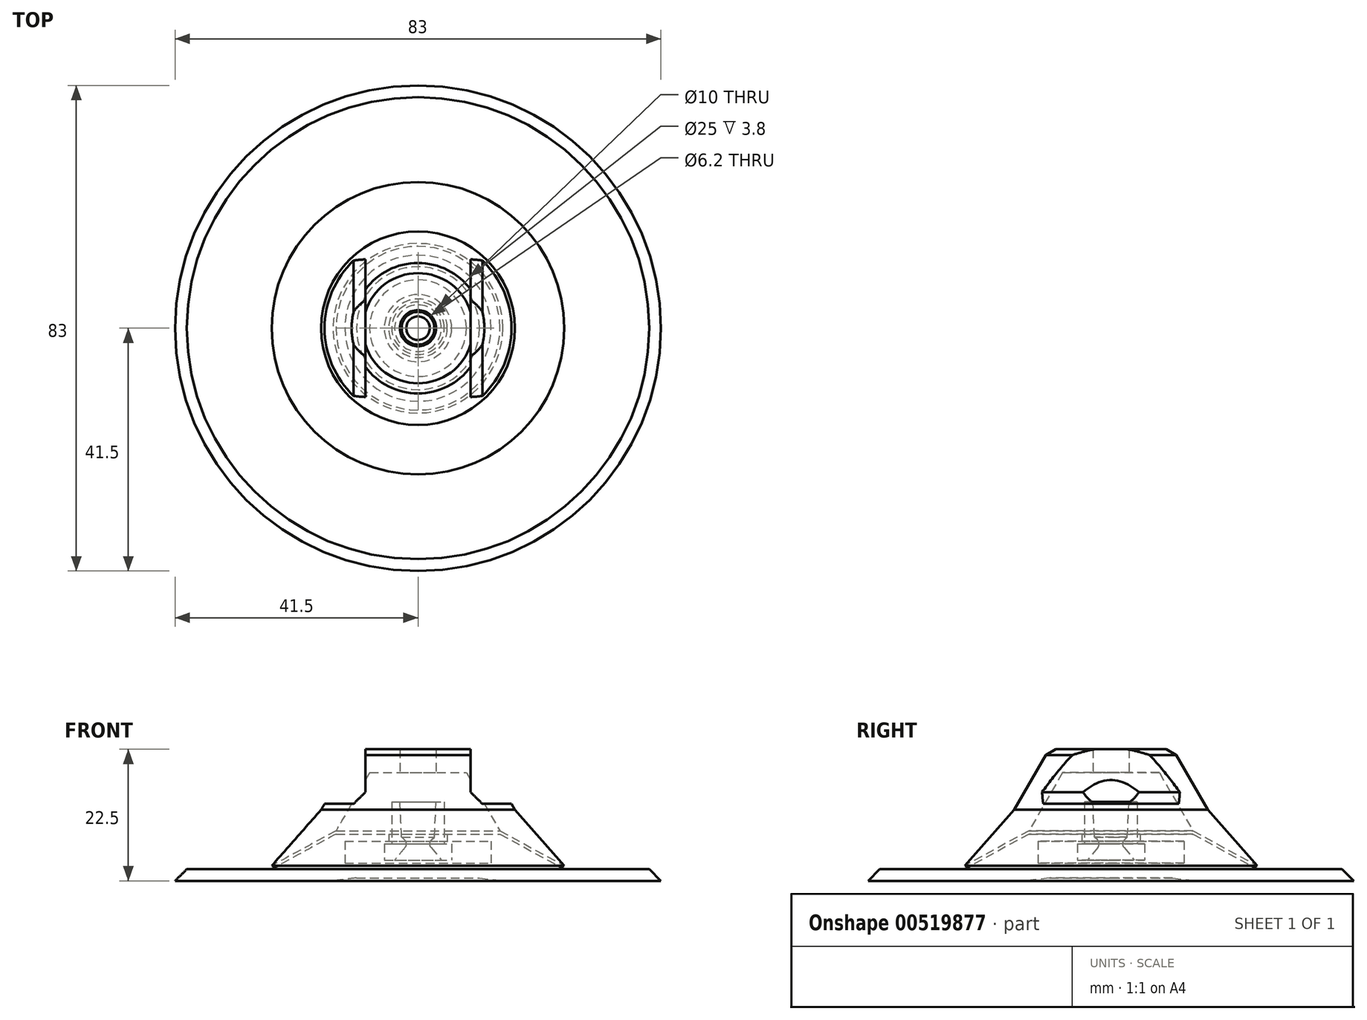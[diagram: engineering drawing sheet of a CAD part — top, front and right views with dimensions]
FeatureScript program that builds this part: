
annotation { "Feature Type Name" : "Feature", "Feature Type Description" : "" }
export const myFeature = defineFeature(function(context is Context, id is Id, definition is map)
    precondition{}
    {
        {
            var Q0;
            Q0=qCreatedBy(makeId("Front.planeOp"),FACE);
            var sketch = newSketch(context, id + "F0", { "sketchPlane" : qUnion([Q0])});
            skLineSegment(sketch, "E0", {"start": v(0, 0) * mm, "end": v(0, 41.16) * mm});
            skLineSegment(sketch, "E1", {"start": v(0, 0.5) * mm, "end": v(10.5, 0.5) * mm});
            skLineSegment(sketch, "E2", {"start": v(10.5, 0.5) * mm, "end": v(14.5, 0) * mm});
            skLineSegment(sketch, "E3", {"start": v(14.5, 0) * mm, "end": v(41.5, 0) * mm});
            skLineSegment(sketch, "E4", {"start": v(41.5, 0) * mm, "end": v(39.5, 2) * mm});
            skLineSegment(sketch, "E5", {"start": v(39.5, 2) * mm, "end": v(25, 2) * mm});
            skLineSegment(sketch, "E6", {"start": v(25, 2) * mm, "end": v(14, 8) * mm});
            skLineSegment(sketch, "E7", {"start": v(14, 8) * mm, "end": v(5, 8) * mm});
            skLineSegment(sketch, "E8", {"start": v(5, 8) * mm, "end": v(5, 6.8) * mm});
            skLineSegment(sketch, "E9", {"start": v(5, 6.8) * mm, "end": v(12.5, 6.8) * mm});
            skLineSegment(sketch, "E10", {"start": v(12.5, 6.8) * mm, "end": v(12.5, 3) * mm});
            skLineSegment(sketch, "E11", {"start": v(12.5, 3) * mm, "end": v(0, 3) * mm});
            skSolve(sketch);
        }
        {
            var Q0;
            Q0=qCreatedBy(makeId("Front.planeOp"),FACE);
            var sketch = newSketch(context, id + "F1", { "sketchPlane" : qUnion([Q0])});
            skLineSegment(sketch, "E12", {"start": v(4.5, 6.3) * mm, "end": v(5.75, 6.3) * mm});
            skLineSegment(sketch, "E13", {"start": v(5.75, 6.3) * mm, "end": v(5.75, 3.5) * mm});
            skLineSegment(sketch, "E14", {"start": v(5.75, 3.5) * mm, "end": v(0, 3.5) * mm});
            skLineSegment(sketch, "E15", {"start": v(0, 3.5) * mm, "end": v(0, 13.5) * mm});
            skLineSegment(sketch, "E16", {"start": v(0, 13.5) * mm, "end": v(4.5, 13.5) * mm});
            skLineSegment(sketch, "E17", {"start": v(4.5, 13.5) * mm, "end": v(4.5, 6.3) * mm});
            skLineSegment(sketch, "E18", {"start": v(3.1, 13.5) * mm, "end": v(2.8, 7.5) * mm});
            skLineSegment(sketch, "E19", {"start": v(2.8, 7.5) * mm, "end": v(0, 7.5) * mm});
            skLineSegment(sketch, "E20", {"start": v(25, 2.57) * mm, "end": v(14, 8.57) * mm});
            skLineSegment(sketch, "E21", {"start": v(14, 8.57) * mm, "end": v(8.27, 18.5) * mm});
            skLineSegment(sketch, "E22", {"start": v(8.27, 18.5) * mm, "end": v(3.1, 18.5) * mm});
            skLineSegment(sketch, "E23", {"start": v(3.1, 18.5) * mm, "end": v(3.1, 22.5) * mm});
            skLineSegment(sketch, "E24", {"start": v(3.1, 22.5) * mm, "end": v(10.58, 22.5) * mm});
            skLineSegment(sketch, "E25", {"start": v(10.58, 22.5) * mm, "end": v(16.54, 12.17) * mm});
            skLineSegment(sketch, "E26", {"start": v(16.54, 12.17) * mm, "end": v(25, 2.57) * mm});
            skLineSegment(sketch, "E27", {"start": v(0, 8.5) * mm, "end": v(4, 3.5) * mm});
            skLineSegment(sketch, "E28", {"start": v(2.8, 7.5) * mm, "end": v(1.69, 6.39) * mm});
            skSolve(sketch);
        }
        {
            var Q0;
            Q0=makeQuery(id+"F1.imprint","IMPRINT",FACE,{"disambiguationData":[TD([[makeQuery(id+"F1.imprint","IMPRINT",EDGE,{"derivedFrom":sQuery(id+"F1.wireOp",EDGE,"E20")}),-1.0]])]});
            var Q1;
            Q1=makeQuery(id+"F1.imprint","IMPRINT",FACE,{"disambiguationData":[TD([[makeQuery(id+"F1.imprint","IMPRINT",EDGE,{"derivedFrom":sQuery(id+"F1.wireOp",EDGE,"E12")}),-1.0]])]});
            var Q2;
            {var subQ0=sQuery(id+"F0.wireOp",EDGE,"E1");Q2=makeQuery(id+"F0.imprint","IMPRINT",FACE,{"disambiguationData":[TD([[makeQuery(id+"F0.imprint","IMPRINT",EDGE,{"derivedFrom":subQ0}),1.0]])]});}
            var Q3;
            Q3=sQuery(id+"F0.wireOp",EDGE,"E0");
            revolve(context, id + "F2", {"entities" : qUnion([Q0, Q1, Q2]), "axis" : qUnion([Q3]), "revolveType" : RevolveType.FULL});
        }
        {
            var Q0;
            Q0=makeQuery(id+"F2.opRevolve","SWEPT_EDGE",EDGE,{"disambiguationData":[OSD([sQuery(id+"F1.wireOp",EDGE,"E27"),sQuery(id+"F1.wireOp",EDGE,"E28")])]});
            fillet(context, id + "F3", {"entities" : qUnion([Q0]), "radius" : 1 * mm, "tangentPropagation" : true, "allowEdgeOverflow" : false});
        }
        {
            var Q0;
            Q0=qCreatedBy(makeId("Front.planeOp"),FACE);
            var sketch = newSketch(context, id + "F4", { "sketchPlane" : qUnion([Q0])});
            skLineSegment(sketch, "E29", {"start": v(0, 0) * mm, "end": v(0, 41.76) * mm, "construction": true});
            skSolve(sketch);
        }
        {
            var Q0;
            Q0=qCreatedBy(makeId("Front.planeOp"),FACE);
            var sketch = newSketch(context, id + "F5", { "sketchPlane" : qUnion([Q0])});
            skLineSegment(sketch, "E30", {"start": v(9, 58.63) * mm, "end": v(9, 13.17) * mm});
            skLineSegment(sketch, "E31", {"start": v(9, 13.17) * mm, "end": v(35.37, 13.17) * mm});
            skLineSegment(sketch, "E32", {"start": v(35.37, 13.17) * mm, "end": v(9, 58.63) * mm});
            skLineSegment(sketch, "E33.MirrorCS", {"start": v(-9, 58.63) * mm, "end": v(-9, 13.17) * mm});
            skLineSegment(sketch, "E34.MirrorCS", {"start": v(-9, 13.17) * mm, "end": v(-35.37, 13.17) * mm});
            skLineSegment(sketch, "E35.MirrorCS", {"start": v(-35.37, 13.17) * mm, "end": v(-9, 58.63) * mm});
            skSolve(sketch);
        }
        {
            var Q0;
            Q0 = qSketchRegion(id + "F5", true);
            extrude(context, id + "F6", {"entities" : qUnion([Q0]), "operationType" : NewBodyOperationType.REMOVE, "endBound" : BoundingType.SYMMETRIC, "oppositeDirection" : true, "depth" : 30 * mm, "offsetDistance" : 25 * mm});
        }
        {
            var Q0;
            Q0=makeQuery(id+"F6.boolean.opBoolean","COPY",EDGE,{"disambiguationData":[OD(0.0)],"derivedFrom":makeQuery(id+"F6.opExtrude","SWEPT_EDGE",EDGE,{"disambiguationData":[OSD([sQuery(id+"F5.wireOp",EDGE,"E30"),sQuery(id+"F5.wireOp",EDGE,"E31")])]})});
            var Q1;
            Q1=makeQuery(id+"F6.boolean.opBoolean","COPY",EDGE,{"disambiguationData":[OD(1.0)],"derivedFrom":makeQuery(id+"F6.opExtrude","SWEPT_EDGE",EDGE,{"disambiguationData":[OSD([sQuery(id+"F5.wireOp",EDGE,"E30"),sQuery(id+"F5.wireOp",EDGE,"E31")])]})});
            var Q2;
            Q2=makeQuery(id+"F6.boolean.opBoolean","COPY",EDGE,{"disambiguationData":[OD(1.0)],"derivedFrom":makeQuery(id+"F6.opExtrude","SWEPT_EDGE",EDGE,{"disambiguationData":[OSD([sQuery(id+"F5.wireOp",EDGE,"E33.MirrorCS"),sQuery(id+"F5.wireOp",EDGE,"E34.MirrorCS")])]})});
            var Q3;
            Q3=makeQuery(id+"F6.boolean.opBoolean","COPY",EDGE,{"disambiguationData":[OD(0.0)],"derivedFrom":makeQuery(id+"F6.opExtrude","SWEPT_EDGE",EDGE,{"disambiguationData":[OSD([sQuery(id+"F5.wireOp",EDGE,"E33.MirrorCS"),sQuery(id+"F5.wireOp",EDGE,"E34.MirrorCS")])]})});
            var Q4;
            Q4=makeQuery(id+"F6.boolean.opBoolean","SPLIT",EDGE,{"disambiguationData":[OD(0.0)],"derivedFrom":makeQuery(id+"F2.opRevolve","SWEPT_EDGE",EDGE,{"disambiguationData":[OSD([sQuery(id+"F1.wireOp",EDGE,"E24"),sQuery(id+"F1.wireOp",EDGE,"E25")])]})});
            var Q5;
            Q5=makeQuery(id+"F6.boolean.opBoolean","SPLIT",EDGE,{"disambiguationData":[OD(1.0)],"derivedFrom":makeQuery(id+"F2.opRevolve","SWEPT_EDGE",EDGE,{"disambiguationData":[OSD([sQuery(id+"F1.wireOp",EDGE,"E24"),sQuery(id+"F1.wireOp",EDGE,"E25")])]})});
            chamfer(context, id + "F7", {"entities" : qUnion([Q0, Q1, Q2, Q3, Q4, Q5]), "width" : 2 * mm, "tangentPropagation" : true});
        }
    });
